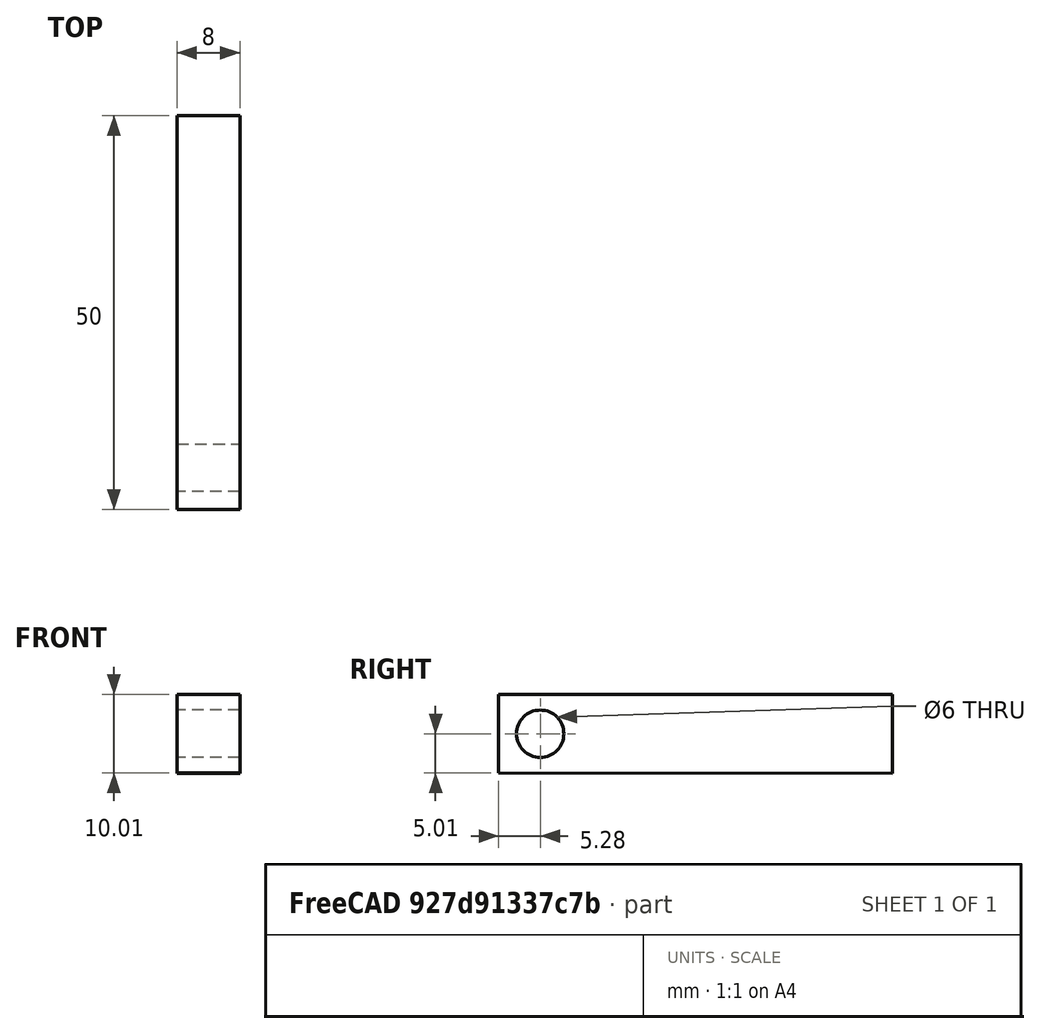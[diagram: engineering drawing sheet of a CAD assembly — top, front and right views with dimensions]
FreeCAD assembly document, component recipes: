
FREECAD ASSEMBLY — COMPONENT RECIPES ("Assembly_001")

This assembly document has 2 components, labeled P0..P1 below (a component is one placed body or linked part). 1 of them carries a construction recipe — the FreeCAD feature program that regenerates the part from scratch, quoted from this document or its linked companion documents; the rest are supplied as boundary geometry only. No exploded tour is included for this assembly.
COMPONENT P0 — geometry summary ("Assembly"; no construction recipe available for this part):
  bounding box: 46.3 x 46.3 x 16.0 mm
  tessellated surface: 64 triangles
  volume: 305088362615919171547142648097323441531641207906357228379628773069613019798462884296926676273468538880 mm^3 (888393614716927035359192664234339284186522147022723223109614180533399636108623982268840037943607296% of its bounding box)
COMPONENT P1 — recipe-attached ("Body", modeled in this document).
Construction recipe (the document's own serialized feature program — sketch geometry with constraints, then the solid features built on it; lengths are millimeters unless a unit is written):

FEATURE [PartDesign::CoordinateSystem] LCS_0
  AttacherType = Attacher::AttachEngine3D
  MapMode = 2
  Support = -> [X_Axis001]
FEATURE [Sketcher::SketchObject] Sketch
  FullyConstrained = false
  MapMode = 5
  Placement = pos=(0,0,0) rot=(0.57735,0.57735,0.57735;2.0944rad)
  Support = -> [YZ_Plane001]
  sketch-geometry (5):
    g0: LineSegment StartX=-5.27726 StartY=5.00146 StartZ=0 EndX=44.7227 EndY=4.98767 EndZ=0
    g1: LineSegment StartX=44.7227 StartY=4.98767 StartZ=0 EndX=44.72 EndY=-5.01233 EndZ=0
    g2: LineSegment StartX=44.72 StartY=-5.01233 StartZ=0 EndX=-5.28002 EndY=-4.99854 EndZ=0
    g3: LineSegment StartX=-5.28002 StartY=-4.99854 StartZ=0 EndX=-5.27726 EndY=5.00146 EndZ=0
    g4: Circle CenterX=0 CenterY=0 CenterZ=0 NormalX=0 NormalY=0 NormalZ=1 AngleXU=0 Radius=3
  constraints (13):
    c: Coincident(g0,g1)
    c: Coincident(g1,g2)
    c: Coincident(g2,g3)
    c: Coincident(g3,g0)
    c: Distance(g0,g2) = 10
    c: Distance(g0,g0) = 50
    c: Parallel(g0,g2)
    c: Parallel(g3,g1)
    c: Perpendicular(g0,g1)
    c: Coincident(g4,g-1)
    c: Radius(g4) = 3
    c: Distance(g4,g0) = 45
    c: Distance(g4,g1) = 45
FEATURE [PartDesign::Pad] Pad
  Direction = (1,-2e-16,3e-16)
  Length = 8
  Length2 = 10
  Placement = pos=(0,0,0) rot=(0.57735,0.57735,0.57735;2.0944rad)
  Profile = -> Sketch
  ReferenceAxis = -> Sketch [N_Axis]
  Type = 0
FEATURE [PartDesign::Body] Body
  Group = -> [LCS_0,Sketch,Pad]
  Origin = -> Origin001
  Placement = pos=(-52,0,0) rot=(0,0,1;0rad)
  Tip = -> Pad
PROVENANCE & LICENSES
A FreeCAD (.FCStd) document from a public repository crawl; recipes are the document's own serialized feature recipes (and, for linked parts, companion documents' recipes).
License: as declared in the source repository (recorded in the dataset sidecar).
